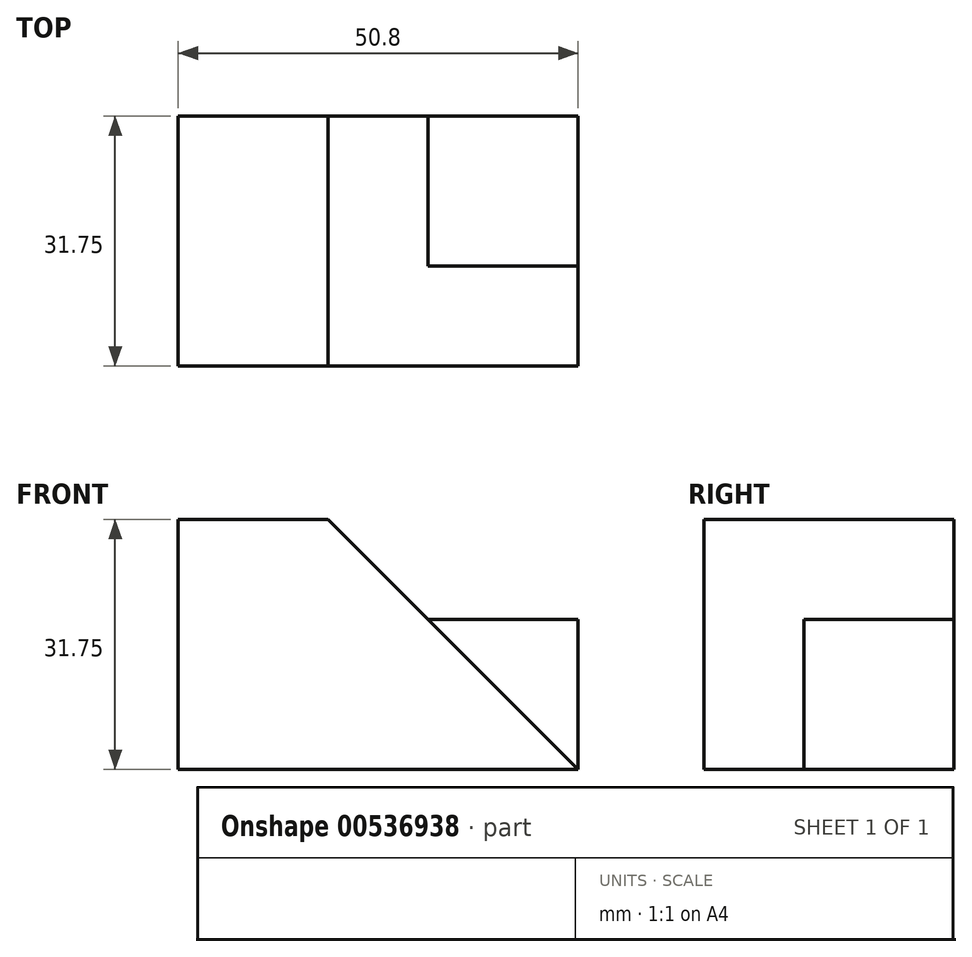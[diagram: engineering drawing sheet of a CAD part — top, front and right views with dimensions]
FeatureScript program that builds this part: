
annotation { "Feature Type Name" : "Feature", "Feature Type Description" : "" }
export const myFeature = defineFeature(function(context is Context, id is Id, definition is map)
    precondition{}
    {
        {
            var Q0;
            Q0=qCreatedBy(makeId("Front.planeOp"),FACE);
            var sketch = newSketch(context, id + "F0", { "sketchPlane" : qUnion([Q0])});
            skLineSegment(sketch, "E0.bottom", {"start": v(-38.81, 21.2) * mm, "end": v(11.99, 21.2) * mm});
            skLineSegment(sketch, "E0.top", {"start": v(-38.81, -10.56) * mm, "end": v(11.99, -10.56) * mm});
            skLineSegment(sketch, "E0.left", {"start": v(-38.81, 21.2) * mm, "end": v(-38.81, -10.56) * mm});
            skLineSegment(sketch, "E0.right", {"start": v(11.99, 21.2) * mm, "end": v(11.99, -10.56) * mm});
            skSolve(sketch);
        }
        {
            var Q0;
            Q0=makeQuery(id+"F0.imprint","IMPRINT",FACE,{"disambiguationData":[TD([[makeQuery(id+"F0.imprint","IMPRINT",EDGE,{"derivedFrom":sQuery(id+"F0.wireOp",EDGE,"E0.bottom")}),-1.0]])]});
            extrude(context, id + "F1", {"entities" : qUnion([Q0]), "depth" : 31.75 * mm, "offsetDistance" : 25.4 * mm});
        }
        {
            var Q0;
            Q0=makeQuery(id+"F1.opExtrude","CAP_FACE",FACE,{"disambiguationData":[OSD([sQuery(id+"F0.wireOp",EDGE,"E0.bottom"),sQuery(id+"F0.wireOp",EDGE,"E0.top"),sQuery(id+"F0.wireOp",EDGE,"E0.left"),sQuery(id+"F0.wireOp",EDGE,"E0.right")])],"isStart":false});
            var sketch = newSketch(context, id + "F2", { "sketchPlane" : qUnion([Q0])});
            skLineSegment(sketch, "E1", {"start": v(11.99, -10.56) * mm, "end": v(-19.76, 21.2) * mm});
            skLineSegment(sketch, "E2", {"start": v(-19.76, 21.2) * mm, "end": v(11.99, 21.2) * mm});
            skLineSegment(sketch, "E3", {"start": v(11.99, 21.2) * mm, "end": v(11.99, -10.56) * mm});
            skSolve(sketch);
        }
        {
            var Q0;
            Q0=makeQuery(id+"F2.imprint","IMPRINT",FACE,{"disambiguationData":[TD([[makeQuery(id+"F2.imprint","IMPRINT",EDGE,{"derivedFrom":sQuery(id+"F2.wireOp",EDGE,"E1")}),-1.0]])]});
            extrude(context, id + "F3", {"entities" : qUnion([Q0]), "operationType" : NewBodyOperationType.REMOVE, "oppositeDirection" : true, "depth" : 12.7 * mm, "offsetDistance" : 25.4 * mm});
        }
        {
            var Q0;
            Q0=makeQuery(id+"F1.opExtrude","CAP_FACE",FACE,{"disambiguationData":[OSD([sQuery(id+"F0.wireOp",EDGE,"E0.bottom"),sQuery(id+"F0.wireOp",EDGE,"E0.top"),sQuery(id+"F0.wireOp",EDGE,"E0.left"),sQuery(id+"F0.wireOp",EDGE,"E0.right")])],"isStart":true});
            var sketch = newSketch(context, id + "F4", { "sketchPlane" : qUnion([Q0])});
            skPoint(sketch, "E4.end.orphan", {"position": v(0, 8.5) * mm});
            skPoint(sketch, "E4.start.orphan", {"position": v(-11.99, 8.5) * mm});
            skLineSegment(sketch, "E5", {"start": v(-11.99, 8.5) * mm, "end": v(7.06, 8.5) * mm});
            skLineSegment(sketch, "E6", {"start": v(7.06, 8.5) * mm, "end": v(19.76, 21.2) * mm});
            skSolve(sketch);
        }
        {
            var Q0;
            {var subQ0=sQuery(id+"F4.wireOp",EDGE,"E5");Q0=makeQuery(id+"F4.imprint","IMPRINT",FACE,{"disambiguationData":[TD([[makeQuery(id+"F4.imprint","IMPRINT",EDGE,{"derivedFrom":subQ0}),1.0]])]});}
            extrude(context, id + "F5", {"entities" : qUnion([Q0]), "operationType" : NewBodyOperationType.REMOVE, "oppositeDirection" : true, "depth" : 31.75 * mm, "offsetDistance" : 25.4 * mm});
        }
    });
